# Revit family: 15-7196-14-MS
name_source: partatom
category: Luminarias
revit_build: Autodesk Revit 2017 (Build: 20160225_1515(x64)
units: mm (PartAtom-declared; Revit-internal decimal feet)

## family parameters
Anfitrión = Cara
Compartido = Sí
Corte con vacíos al cargar = No
Cota de conector redondo = Diámetro de uso
Número OmniClass = 23.80.70.00
Origen de luz = No
Punto de cálculo de habitación = No
Tipo de pieza = Normal
Título OmniClass = Lighting

## types (1)
- 15-7196-14-MS
    Acabado = Blanco
    CRI = 90
    Carga aparente = 0 VA
    Catálogo = Technical
    CodigoGubimclass = 50.60.50.20
    CodigoOmniclass = 21-04 50 40
    CodigoUniclass2015 = EF_70_80
    CodigoUniformat2010 = D5040
    DescripcionGubimclass = Iluminación interior
    DescripcionOmniclass = Lighting
    DescripcionUniclass2015 = Lighting
    DescripcionUniformat2010 = Lighting
    EAN13 = 8435526869299
    Eficiencia energética = LED A++
    Elevación por defecto = 1000 mm  [stored 3.28084 ft]
    Etiqueta V/f = 220-240V/50-60Hz
    Fabricante = LEDS C4
    Familia = Bento Surface 12 LEDS
    FechaVersion = Julio 2020
    Ficha = http://files.leds-c4.com
    Fotometría = http://files.leds-c4.com
    Fuente de luz = 12xLED 24.4 2160.00 lm
    IMC = http://files.leds-c4.com
    IP = IP23
    IfcExportAs = IfcLightFixture
IfcLightFixture
    IfcExportType = NOTDEFINED
    Imagen web = http://files.leds-c4.com
    LDT = http://files.leds-c4.com
    Lumenes reales (lm) = 1744
    Material = Aluminio
    Peso neto (KG) = 0.72
    Pluma comercial = http://files.leds-c4.com
    Producto descatalogado = Catalogado ES
    Rayo de luz = EXTRA SPOT
    Referencia = 15-7196-14-MS
    Temperatura color led (K) = Blanco cálido - 2700K
    Tender text (Castellano) = LEDS C4
Bento Surface 12 LEDS
15-7196-14-MS

Plafón de uso interior para iluminar hacia abajo. 

UGR &lt;10. Material estructura: Aluminio. Acabado estructura: Blanco. Garantía: 5 Años.

Peso neto del producto (Kg): 0.720
Longitud del producto (mm): 322.5
Anchura o diámetro del producto (mm): 35.8
Altura del producto (mm): 85

Clase 2. IP: IP23. LED. Nº de portalámparas o Leds: 12. Marca del LED: NICHIA. Marca del Driver: ELT. Potencia máxima de la fuente de luz: 24.4W. Temperatura de color: Blanco cálido - 2700K. Índice de reproducción cromática: 90. Steps Mac Adam: 3. Diámetro máximo de la bombilla que admite la luminaria: 50.000h L80B20. Riesgo fotobiológico: RG2. Flujo real (lm): 1744. Flujo nominal (lm): 2160. Lm/W reales: 68. Rango de voltaje/frecuencia: 198-264/50-60Hz. Voltaje: 3. Equipo incluido: Si, electrónico. Potencia total: 25.7. Factor de potencia: 0.90. Equipo regulable incluido: TRIAC.
    Tender text (English) = LEDS C4
Bento Surface 12 LEDS
15-7196-14-MS

Recessed light fitting for indoor use. 

For downlighting. UGR &lt;10. Structure material: Aluminium. Structure finish: White. Warranty: 5 Years.

Product net weight (Kg): 0.720
Product length (mm): 322.5
Product width or diameter (mm): 35.8
Product height (mm): 85

Class 2. IP: IP23. LED. No. of lampholders or LEDs: 12. LED brand: NICHIA. Driver brand: ELT. Maximum power of light source: 24.4W. Colour temperature: LED warm-white 2700K. Colour rendering index: 90. MacAdam Steps: 3. Maximum diameter of luminaire bulb: 50.000h L80B20. Photobiological risk: RG2. Real flux (lm): 1744. Nominal flux (lm): 2160. Lm/Real W: 68. Voltage and frequency range: 198-264/50-60Hz. Voltage: 3. Gear included: Yes, electronic. Total power: 25.7. Power factor: 0.90. Dimmable gear included: TRIAC.
    Tipo = Plafon
    Tipo de regulación = TRIAC
    Vatios (W) = 25.7
    Versión = v1

note: [stored X ft] marks values corroborated as IEEE doubles in the binary element streams (Revit-internal decimal feet)
